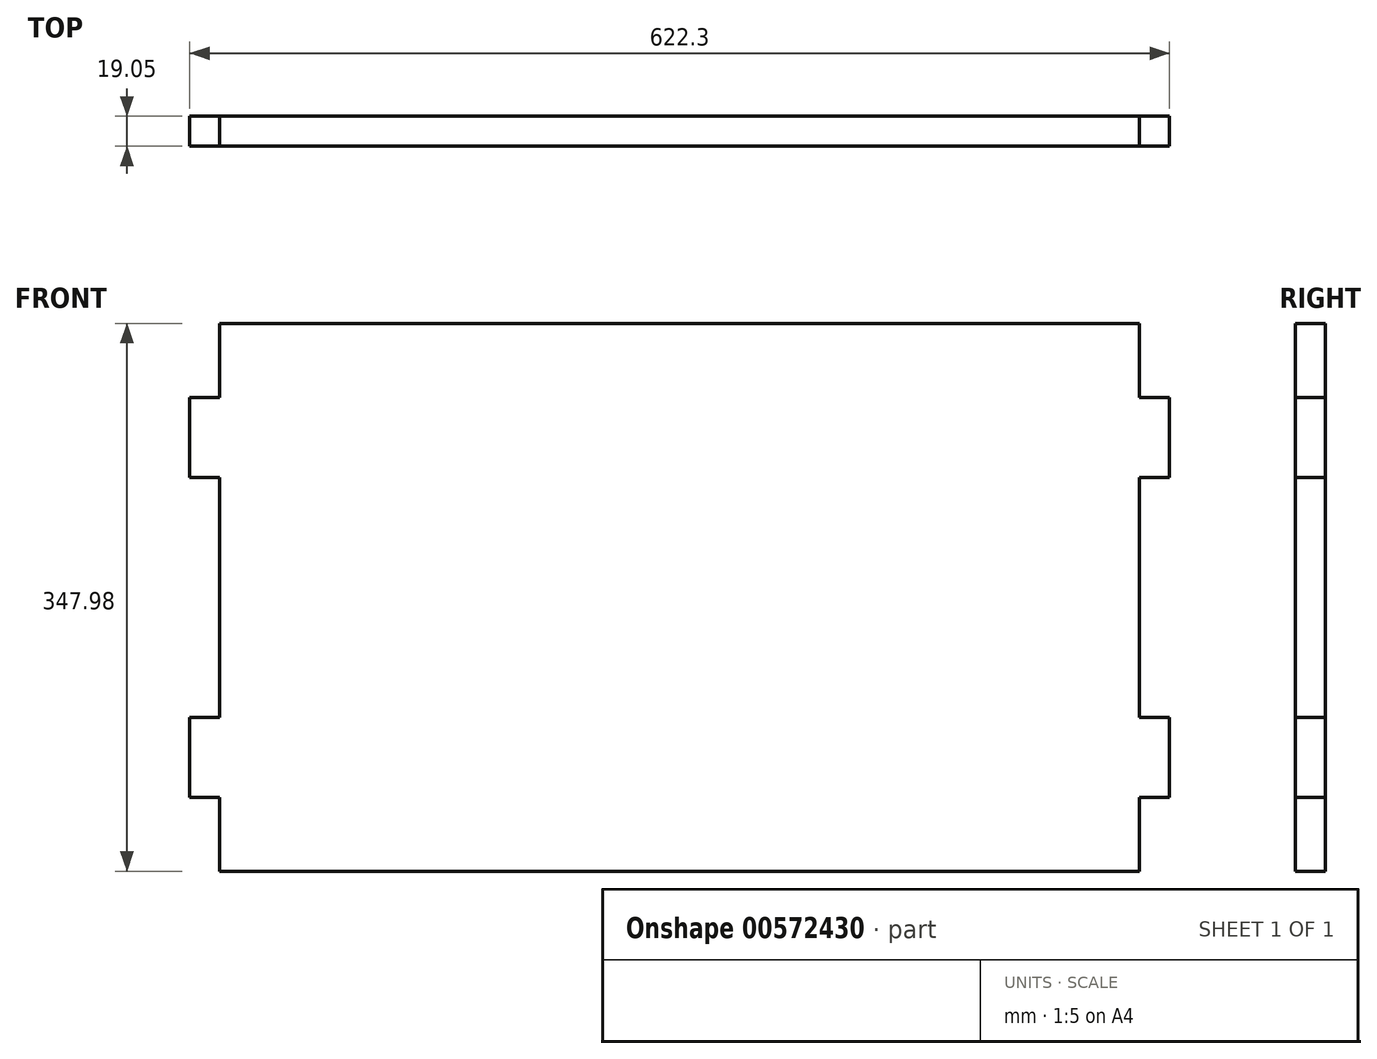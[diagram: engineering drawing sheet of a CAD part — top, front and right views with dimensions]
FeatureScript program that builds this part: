
annotation { "Feature Type Name" : "Feature", "Feature Type Description" : "" }
export const myFeature = defineFeature(function(context is Context, id is Id, definition is map)
    precondition{}
    {
        {
            var Q0;
            Q0=qCreatedBy(makeId("Front.planeOp"),FACE);
            var sketch = newSketch(context, id + "F0", { "sketchPlane" : qUnion([Q0])});
            skLineSegment(sketch, "E0.bottom", {"start": v(0, 0) * mm, "end": v(584.2, 0) * mm});
            skLineSegment(sketch, "E0.top", {"start": v(0, 347.98) * mm, "end": v(584.2, 347.98) * mm});
            skLineSegment(sketch, "E0.left", {"start": v(0, 0) * mm, "end": v(0, 46.99) * mm});
            skLineSegment(sketch, "E0.right", {"start": v(584.2, 0) * mm, "end": v(584.2, 46.99) * mm});
            skLineSegment(sketch, "E1", {"start": v(292.1, 347.98) * mm, "end": v(292.1, -296.1) * mm, "construction": true});
            skLineSegment(sketch, "E2", {"start": v(0, 174) * mm, "end": v(768.38, 174) * mm, "construction": true});
            skLineSegment(sketch, "E3.bottom", {"start": v(0, 301) * mm, "end": v(-19.05, 301) * mm});
            skLineSegment(sketch, "E3.top", {"start": v(0, 250.2) * mm, "end": v(-19.05, 250.2) * mm});
            skLineSegment(sketch, "E3.right", {"start": v(-19.05, 301) * mm, "end": v(-19.05, 250.2) * mm});
            skLineSegment(sketch, "E4.MirrorCS", {"start": v(0, 46.99) * mm, "end": v(-19.05, 46.99) * mm});
            skLineSegment(sketch, "E5.MirrorCS", {"start": v(-19.05, 46.99) * mm, "end": v(-19.05, 97.79) * mm});
            skLineSegment(sketch, "E6.MirrorCS", {"start": v(0, 97.79) * mm, "end": v(-19.05, 97.79) * mm});
            skLineSegment(sketch, "E7.MirrorCS", {"start": v(584.2, 301) * mm, "end": v(603.25, 301) * mm});
            skLineSegment(sketch, "E8.MirrorCS", {"start": v(603.25, 301) * mm, "end": v(603.25, 250.2) * mm});
            skLineSegment(sketch, "E9.MirrorCS", {"start": v(584.2, 250.2) * mm, "end": v(603.25, 250.2) * mm});
            skLineSegment(sketch, "E10.MirrorCS", {"start": v(584.2, 97.79) * mm, "end": v(603.25, 97.79) * mm});
            skLineSegment(sketch, "E11.MirrorCS", {"start": v(603.25, 46.99) * mm, "end": v(603.25, 97.79) * mm});
            skLineSegment(sketch, "E12.MirrorCS", {"start": v(584.2, 46.99) * mm, "end": v(603.25, 46.99) * mm});
            skLineSegment(sketch, "E13.trimOffspring", {"start": v(0, 301) * mm, "end": v(0, 347.98) * mm});
            skPoint(sketch, "E14.MirrorCS.end.orphan", {"position": v(0, 97.79) * mm});
            skPoint(sketch, "E14.MirrorCS.start.orphan", {"position": v(0, 46.99) * mm});
            skLineSegment(sketch, "E15.trimOffspring", {"start": v(0, 97.79) * mm, "end": v(0, 250.2) * mm});
            skLineSegment(sketch, "E16.trimOffspring", {"start": v(584.2, 97.79) * mm, "end": v(584.2, 250.2) * mm});
            skLineSegment(sketch, "E17.trimOffspring", {"start": v(584.2, 301) * mm, "end": v(584.2, 347.98) * mm});
            skSolve(sketch);
        }
        {
            var Q0;
            Q0=qSketchRegion(id+"F0",true);
            extrude(context, id + "F1", {"entities" : qUnion([Q0]), "depth" : 19.05 * mm, "offsetDistance" : 25.4 * mm});
        }
    });
